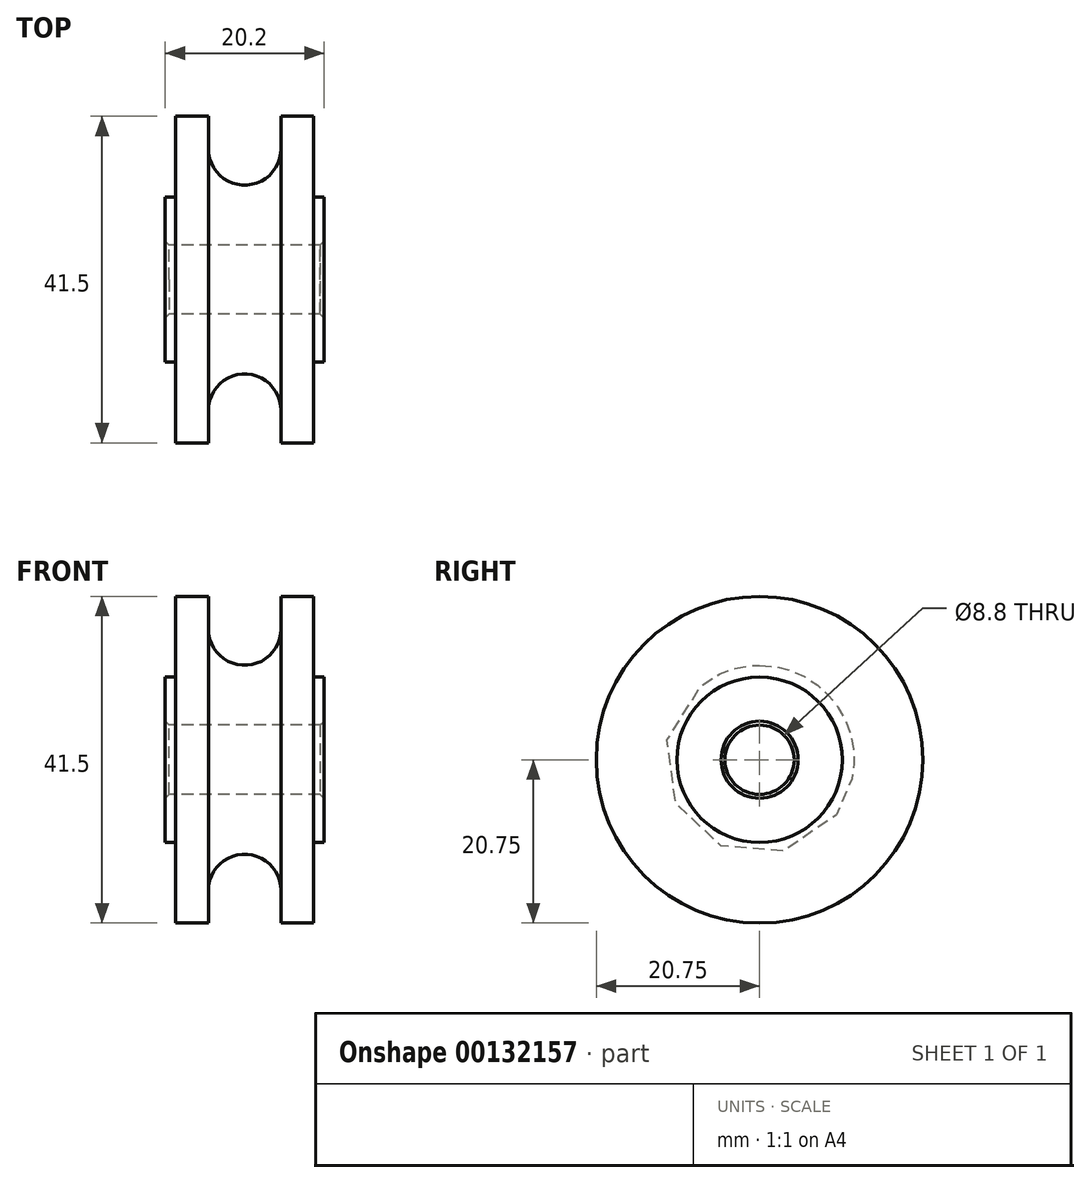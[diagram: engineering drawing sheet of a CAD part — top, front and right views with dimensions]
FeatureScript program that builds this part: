
annotation { "Feature Type Name" : "Feature", "Feature Type Description" : "" }
export const myFeature = defineFeature(function(context is Context, id is Id, definition is map)
    precondition{}
    {
        {
            var Q0;
            Q0=qCreatedBy(makeId("Front.planeOp"),FACE);
            var sketch = newSketch(context, id + "F0", { "sketchPlane" : qUnion([Q0])});
            skLineSegment(sketch, "E0", {"start": v(10.1, 0) * mm, "end": v(10.1, 10.5) * mm});
            skLineSegment(sketch, "E1", {"start": v(10.1, 10.5) * mm, "end": v(8.75, 10.5) * mm});
            skLineSegment(sketch, "E2", {"start": v(8.75, 10.5) * mm, "end": v(8.75, 20.75) * mm});
            skLineSegment(sketch, "E3", {"start": v(8.75, 20.75) * mm, "end": v(4.6, 20.75) * mm});
            skLineSegment(sketch, "E4", {"start": v(4.6, 20.75) * mm, "end": v(4.6, 16.6) * mm});
            skLineSegment(sketch, "E5", {"start": v(0, 0) * mm, "end": v(0, 16.6) * mm, "construction": true});
            skArc(sketch, "E6", {"start": v(0, 12) * mm, "mid": v(3.25, 13.35) * mm, "end": v(4.6, 16.6) * mm});
            skLineSegment(sketch, "E7", {"start": v(0, 12) * mm, "end": v(-9.12, 12) * mm, "construction": true});
            skLineSegment(sketch, "E8", {"start": v(0, 0) * mm, "end": v(10.1, 0) * mm, "construction": true});
            skLineSegment(sketch, "E9", {"start": v(0, 12) * mm, "end": v(0, 0) * mm});
            skLineSegment(sketch, "E10", {"start": v(0, 4.4) * mm, "end": v(10.1, 4.4) * mm});
            skSolve(sketch);
        }
        {
            var Q0;
            Q0=makeQuery(id+"F0.imprint","IMPRINT",FACE,{"disambiguationData":[TD([[makeQuery(id+"F0.imprint","IMPRINT",EDGE,{"derivedFrom":sQuery(id+"F0.wireOp",EDGE,"E0")}),1.0]])]});
            var Q1;
            Q1=sQuery(id+"F0.wireOp",EDGE,"E8");
            revolve(context, id + "F1", {"entities" : qUnion([Q0]), "axis" : qUnion([Q1]), "revolveType" : RevolveType.FULL});
        }
        {
            var Q0;
            Q0=makeQuery(id+"F1.opRevolve","SWEPT_BODY",BODY,{"disambiguationData":[OSD([sQuery(id+"F0.wireOp",EDGE,"E0"),sQuery(id+"F0.wireOp",EDGE,"E1"),sQuery(id+"F0.wireOp",EDGE,"E2"),sQuery(id+"F0.wireOp",EDGE,"E3"),sQuery(id+"F0.wireOp",EDGE,"E4"),sQuery(id+"F0.wireOp",EDGE,"E6"),sQuery(id+"F0.wireOp",EDGE,"E9"),sQuery(id+"F0.wireOp",EDGE,"i9R4IJfn-28pk-aFpj-s5ex-dltPIMKg4rxF")])]});
            var Q1;
            Q1=qCreatedBy(makeId("Right.planeOp"),FACE);
            mirror(context, id + "F2", {"operationType" : NewBodyOperationType.ADD, "entities" : qUnion([Q0]), "mirrorPlane" : qUnion([Q1])});
        }
        {
            var Q0;
            Q0=makeQuery(id+"F1.opRevolve","SWEPT_EDGE",EDGE,{"disambiguationData":[OSD([sQuery(id+"F0.wireOp",EDGE,"E0"),sQuery(id+"F0.wireOp",EDGE,"E10")])]});
            var Q1;
            Q1=makeQuery(id+"F2.opPattern","COPY",EDGE,{"derivedFrom":makeQuery(id+"F1.opRevolve","SWEPT_EDGE",EDGE,{"disambiguationData":[OSD([sQuery(id+"F0.wireOp",EDGE,"E0"),sQuery(id+"F0.wireOp",EDGE,"E10")])]}),"instanceName":"1"});
            chamfer(context, id + "F3", {"entities" : qUnion([Q0, Q1]), "width" : 0.5 * mm, "tangentPropagation" : true});
        }
    });
